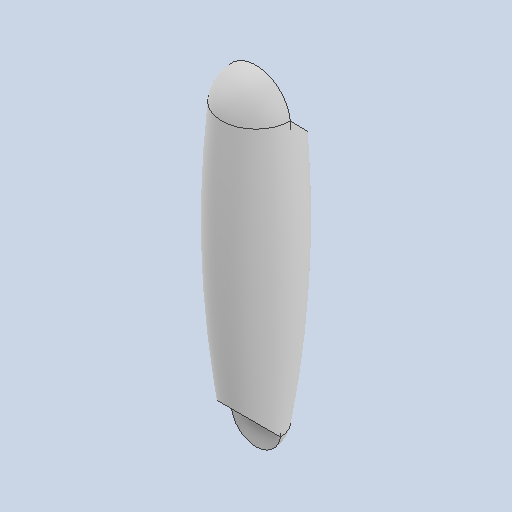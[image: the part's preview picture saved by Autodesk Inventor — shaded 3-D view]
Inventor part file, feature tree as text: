
AUTODESK INVENTOR PART (.ipt)
format: ipt  version: 2024.2 (Build 282272000, 272)  size: 134,144 bytes
history: native  units: mm
features: sketch x3, extrude x2, other x1, revolve x1
ambient origin geometry x8: Origin, YZ Plane, XZ Plane, XY Plane, X Axis, Y Axis, Z Axis, Center Point
bodies: Body1 (feature_tree)
feature tree (7):
  other  "Твердое тело1"
  revolve  "Вращение1"
  extrude  "Выдавливание1"  Depth=104.0mm
  extrude  "Выдавливание2"  Depth=75.0mm
  sketch  "Эскиз1"
  sketch  "Эскиз2"
  sketch  "Эскиз3"
